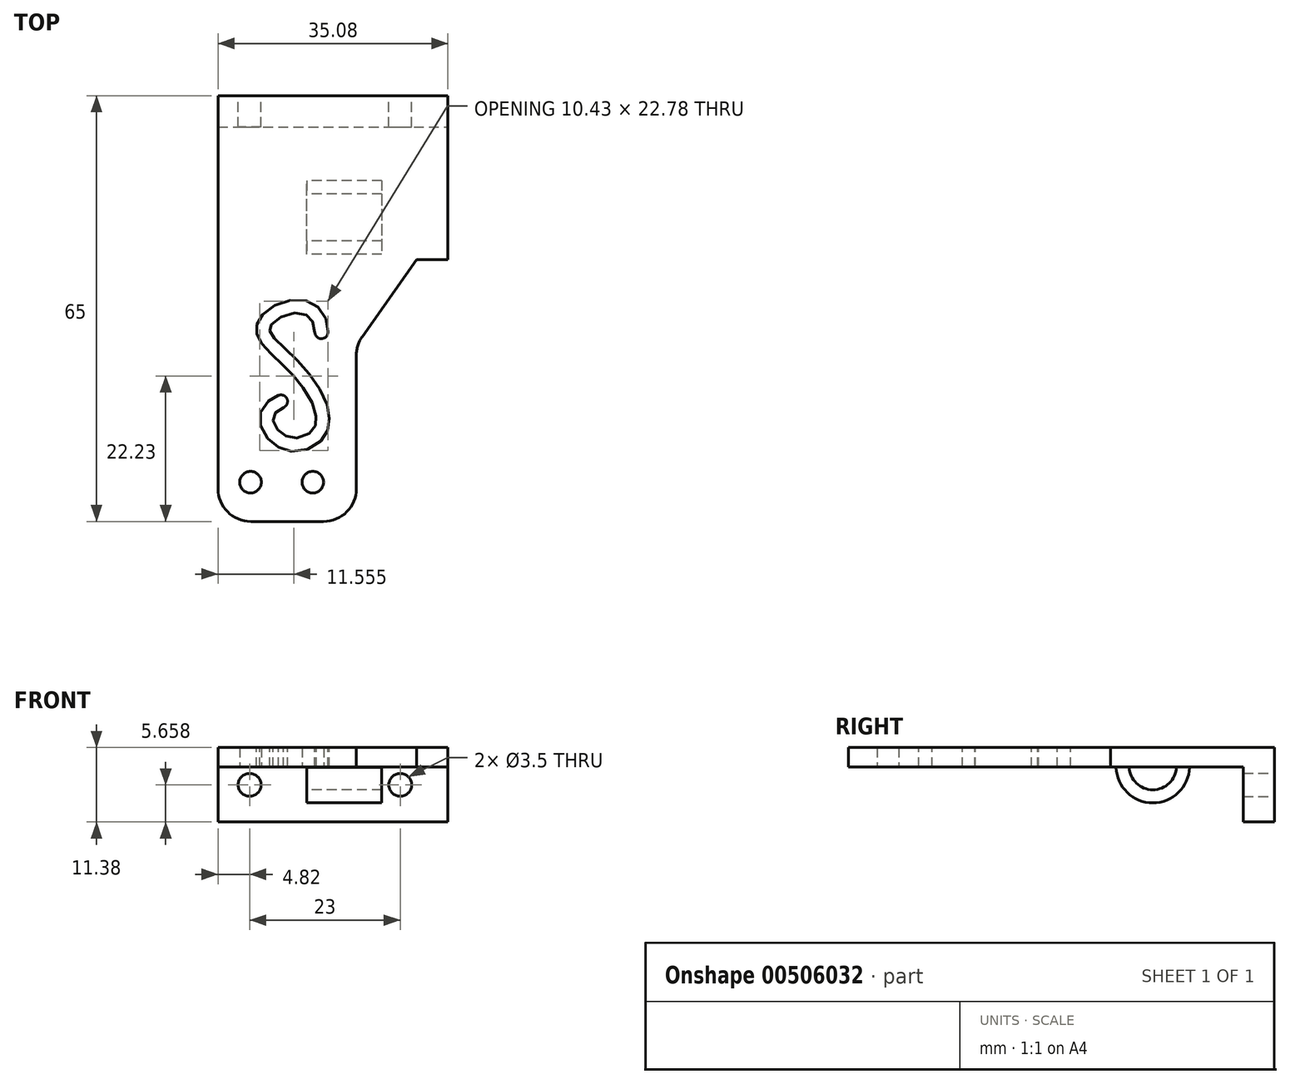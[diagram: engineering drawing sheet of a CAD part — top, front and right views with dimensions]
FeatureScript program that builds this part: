
annotation { "Feature Type Name" : "Feature", "Feature Type Description" : "" }
export const myFeature = defineFeature(function(context is Context, id is Id, definition is map)
    precondition{}
    {
        {
            var Q0;
            Q0=qCreatedBy(makeId("Top.planeOp"),FACE);
            var sketch = newSketch(context, id + "F0", { "sketchPlane" : qUnion([Q0])});
            skLineSegment(sketch, "E0", {"start": v(0, 7.37) * mm, "end": v(-30.32, 7.37) * mm});
            skLineSegment(sketch, "E1", {"start": v(-30.32, 7.37) * mm, "end": v(-30.32, -32.63) * mm});
            skLineSegment(sketch, "E2", {"start": v(-30.32, -32.63) * mm, "end": v(-9.2, -32.63) * mm});
            skLineSegment(sketch, "E3", {"start": v(-9.2, -32.63) * mm, "end": v(-9.2, -5.67) * mm});
            skLineSegment(sketch, "E4", {"start": v(-9.2, -5.67) * mm, "end": v(0, 7.37) * mm});
            skLineSegment(sketch, "E5", {"start": v(-25.36, -26.63) * mm, "end": v(-15.86, -26.63) * mm, "construction": true});
            skSolve(sketch);
        }
        {
            var Q0;
            Q0=makeQuery(id+"F0.imprint","IMPRINT",FACE,{"disambiguationData":[TD([[makeQuery(id+"F0.imprint","IMPRINT",EDGE,{"derivedFrom":sQuery(id+"F0.wireOp",EDGE,"E0")}),1.0]])]});
            extrude(context, id + "F1", {"entities" : qUnion([Q0]), "depth" : 3 * mm});
        }
        {
            var Q0;
            Q0=sQuery(id+"F0.wireOp",VERTEX,"b83b9fe4-897f-4c07-88cb-3c43593c5d40");
            var Q1;
            Q1=sQuery(id+"F0.wireOp",VERTEX,"b232d156-1ebf-488e-844c-e46001ad8d3b");
            var Q2;
            Q2=sQuery(id+"F0.wireOp",VERTEX,"E5.start");
            var Q3;
            Q3=sQuery(id+"F0.wireOp",VERTEX,"E5.end");
            var Q4;
            Q4=makeQuery(id+"F1.opExtrude","SWEPT_BODY",BODY,{"disambiguationData":[OSD([sQuery(id+"F0.wireOp",EDGE,"E0"),sQuery(id+"F0.wireOp",EDGE,"E1"),sQuery(id+"F0.wireOp",EDGE,"E2"),sQuery(id+"F0.wireOp",EDGE,"E3"),sQuery(id+"F0.wireOp",EDGE,"E4")])]});
            hole(context, id + "F2", {"style" : HoleStyle.SIMPLE, "endStyle" : HoleEndStyle.BLIND, "oppositeDirection" : true, "standardTappedOrClearance" : lookupTablePath({ "standard" : "ISO", "fit" : "Normal", "size" : "M3", "type" : "Clearance" }), "standardBlindInLast" : lookupTablePath({ "fit" : "Standard", "standard" : "ISO", "size" : "M3", "type" : "Clearance" }), "holeDiameter" : 3.3 * mm, "holeDepth" : 18 * mm, "isTappedThrough" : true, "tappedDepth" : 12 * mm, "tapClearance" : 3, "startFromSketch" : true, "locations" : qUnion([Q0, Q1, Q2, Q3]), "scope" : qUnion([Q4])});
        }
        {
            var Q0;
            Q0=makeQuery(id+"F1.opExtrude","SWEPT_EDGE",EDGE,{"disambiguationData":[OSD([sQuery(id+"F0.wireOp",EDGE,"E2"),sQuery(id+"F0.wireOp",EDGE,"E3")])]});
            var Q1;
            Q1=makeQuery(id+"F1.opExtrude","SWEPT_EDGE",EDGE,{"disambiguationData":[OSD([sQuery(id+"F0.wireOp",EDGE,"E1"),sQuery(id+"F0.wireOp",EDGE,"E2")])]});
            fillet(context, id + "F3", {"entities" : qUnion([Q0, Q1]), "radius" : 5 * mm, "tangentPropagation" : true, "allowEdgeOverflow" : false});
        }
        {
            var Q0;
            Q0=makeQuery(id+"F1.opExtrude","CAP_FACE",FACE,{"disambiguationData":[OSD([sQuery(id+"F0.wireOp",EDGE,"E0"),sQuery(id+"F0.wireOp",EDGE,"E1"),sQuery(id+"F0.wireOp",EDGE,"E2"),sQuery(id+"F0.wireOp",EDGE,"E3"),sQuery(id+"F0.wireOp",EDGE,"E4")])],"isStart":false});
            var sketch = newSketch(context, id + "F4", { "sketchPlane" : qUnion([Q0])});
            skFitSpline(sketch, "E6", {"points": [v(-14.55, -3.72) * mm, v(-19.67, 0) * mm, v(-23.45, -3.28) * mm, v(-18.59, -9.14) * mm, v(-14.59, -18.4) * mm, v(-20.53, -20.4) * mm, v(-20.71, -14.3) * mm], "startDerivative": vector(-4.14, 69.45) * mm, "endDerivative": vector(70.56, 28.51) * mm});
            skArc(sketch, "E7.0.startCap", {"start": v(-13.55, -3.66) * mm, "mid": v(-14.5, -4.72) * mm, "end": v(-15.55, -3.78) * mm});
            skArc(sketch, "E7.0.endCap", {"start": v(-21.09, -13.38) * mm, "mid": v(-19.79, -13.93) * mm, "end": v(-20.34, -15.23) * mm});
            skFitSpline(sketch, "E7.0.left", {"points": [v(-15.55, -3.78) * mm, v(-15.59, -3.14) * mm, v(-15.76, -2.4) * mm, v(-16.11, -1.76) * mm, v(-16.42, -1.4) * mm, v(-16.76, -1.15) * mm, v(-17.3, -0.9) * mm, v(-18.13, -0.76) * mm, v(-19.27, -0.9) * mm, v(-20.4, -1.26) * mm, v(-21.37, -1.8) * mm, v(-21.96, -2.33) * mm, v(-22.26, -2.73) * mm, v(-22.4, -3) * mm, v(-22.45, -3.23) * mm, v(-22.45, -3.4) * mm, v(-22.4, -3.63) * mm, v(-22.24, -3.94) * mm, v(-22, -4.32) * mm, v(-21.54, -4.87) * mm, v(-20.75, -5.66) * mm, v(-19.59, -6.74) * mm, v(-18.3, -7.96) * mm, v(-17.02, -9.36) * mm, v(-15.82, -10.88) * mm, v(-14.78, -12.48) * mm, v(-13.96, -14.12) * mm, v(-13.51, -15.5) * mm, v(-13.35, -16.6) * mm, v(-13.34, -17.43) * mm, v(-13.46, -18.24) * mm, v(-13.74, -19.03) * mm, v(-14.17, -19.74) * mm, v(-14.9, -20.56) * mm, v(-16.02, -21.35) * mm, v(-17.63, -21.87) * mm, v(-19.07, -21.9) * mm, v(-20.23, -21.63) * mm, v(-21.08, -21.27) * mm, v(-21.86, -20.76) * mm, v(-22.79, -19.9) * mm, v(-23.5, -18.85) * mm, v(-23.88, -17.63) * mm, v(-23.94, -16.65) * mm, v(-23.7, -15.65) * mm, v(-23.14, -14.72) * mm, v(-22.27, -13.95) * mm, v(-21.51, -13.55) * mm, v(-21.09, -13.38) * mm]});
            skFitSpline(sketch, "E7.0.right", {"points": [v(-13.55, -3.66) * mm, v(-13.6, -2.85) * mm, v(-13.83, -1.77) * mm, v(-14.44, -0.63) * mm, v(-15.04, 0.07) * mm, v(-15.74, 0.6) * mm, v(-16.77, 1.06) * mm, v(-18.13, 1.26) * mm, v(-19.72, 1.07) * mm, v(-21.2, 0.59) * mm, v(-22.5, -0.14) * mm, v(-23.4, -0.92) * mm, v(-23.96, -1.66) * mm, v(-24.27, -2.27) * mm, v(-24.42, -2.84) * mm, v(-24.45, -3.32) * mm, v(-24.42, -3.8) * mm, v(-24.27, -4.36) * mm, v(-23.97, -4.97) * mm, v(-23.59, -5.53) * mm, v(-23, -6.24) * mm, v(-22.12, -7.12) * mm, v(-20.95, -8.2) * mm, v(-19.93, -9.18) * mm, v(-19.13, -10.01) * mm, v(-18.36, -10.89) * mm, v(-17.45, -12.05) * mm, v(-16.51, -13.48) * mm, v(-15.8, -14.9) * mm, v(-15.46, -16) * mm, v(-15.35, -16.77) * mm, v(-15.34, -17.3) * mm, v(-15.41, -17.76) * mm, v(-15.56, -18.16) * mm, v(-15.79, -18.55) * mm, v(-16.2, -19.03) * mm, v(-16.92, -19.53) * mm, v(-17.97, -19.87) * mm, v(-18.9, -19.89) * mm, v(-19.6, -19.72) * mm, v(-20.12, -19.5) * mm, v(-20.62, -19.17) * mm, v(-21.09, -18.75) * mm, v(-21.47, -18.26) * mm, v(-21.75, -17.75) * mm, v(-21.9, -17.26) * mm, v(-21.92, -16.81) * mm, v(-21.82, -16.42) * mm, v(-21.6, -16.04) * mm, v(-21.15, -15.63) * mm, v(-20.65, -15.35) * mm, v(-20.34, -15.23) * mm]});
            skSolve(sketch);
        }
        {
            var Q0;
            Q0 = qSketchRegion(id + "F4", true);
            extrude(context, id + "F5", {"entities" : qUnion([Q0]), "operationType" : NewBodyOperationType.REMOVE, "oppositeDirection" : true, "depth" : 25 * mm});
        }
        {
            var Q0;
            Q0=makeQuery(id+"F1.opExtrude","SWEPT_EDGE",EDGE,{"disambiguationData":[OSD([sQuery(id+"F0.wireOp",EDGE,"E3"),sQuery(id+"F0.wireOp",EDGE,"E4")])]});
            fillet(context, id + "F6", {"entities" : qUnion([Q0]), "radius" : 5 * mm, "tangentPropagation" : true, "allowEdgeOverflow" : false});
        }
        {
            var Q0;
            Q0=makeQuery(id+"F1.opExtrude","SWEPT_FACE",FACE,{"disambiguationData":[OSD([sQuery(id+"F0.wireOp",EDGE,"E0")])]});
            var sketch = newSketch(context, id + "F7", { "sketchPlane" : qUnion([Q0])});
            skLineSegment(sketch, "E8.bottom", {"start": v(-4.76, 3) * mm, "end": v(30.32, 3) * mm});
            skLineSegment(sketch, "E8.top", {"start": v(-4.76, -8.38) * mm, "end": v(30.32, -8.38) * mm});
            skLineSegment(sketch, "E8.left", {"start": v(-4.76, 3) * mm, "end": v(-4.76, -8.38) * mm});
            skLineSegment(sketch, "E8.right", {"start": v(30.32, 3) * mm, "end": v(30.32, -8.38) * mm});
            skSolve(sketch);
        }
        {
            var Q0;
            Q0 = qSketchRegion(id + "F7", true);
            extrude(context, id + "F8", {"entities" : qUnion([Q0]), "operationType" : NewBodyOperationType.ADD, "depth" : 25 * mm, "offsetDistance" : 25 * mm});
        }
        {
            var Q0;
            Q0=makeQuery(id+"F8.opExtrude","SWEPT_FACE",FACE,{"disambiguationData":[OSD([sQuery(id+"F7.wireOp",EDGE,"E8.left")])]});
            var sketch = newSketch(context, id + "F9", { "sketchPlane" : qUnion([Q0])});
            skLineSegment(sketch, "E9", {"start": v(27.6, -8.38) * mm, "end": v(27.6, 0) * mm});
            skLineSegment(sketch, "E10", {"start": v(27.6, 0) * mm, "end": v(7.37, 0) * mm});
            skLineSegment(sketch, "E11", {"start": v(7.37, 0) * mm, "end": v(27.6, -8.38) * mm});
            skSolve(sketch);
        }
        {
            var Q0;
            Q0=makeQuery(id+"F9.imprint","IMPRINT",FACE,{"disambiguationData":[TD([[makeQuery(id+"F9.imprint","IMPRINT",EDGE,{"derivedFrom":sQuery(id+"F9.wireOp",EDGE,"E9")}),1.0]])]});
            var Q1;
            {var subQ0=sQuery(id+"F9.wireOp",EDGE,"E11");Q1=makeQuery(id+"F9.imprint","IMPRINT",FACE,{"disambiguationData":[TD([[makeQuery(id+"F9.imprint","IMPRINT",EDGE,{"derivedFrom":subQ0}),-1.0]])]});}
            extrude(context, id + "F10", {"entities" : qUnion([Q0, Q1]), "operationType" : NewBodyOperationType.REMOVE, "oppositeDirection" : true, "depth" : 40 * mm, "offsetDistance" : 25 * mm});
        }
        {
            var Q0;
            Q0=makeQuery(id+"F8.opExtrude","CAP_FACE",FACE,{"disambiguationData":[OSD([sQuery(id+"F7.wireOp",EDGE,"E8.bottom"),sQuery(id+"F7.wireOp",EDGE,"E8.top"),sQuery(id+"F7.wireOp",EDGE,"E8.left"),sQuery(id+"F7.wireOp",EDGE,"E8.right")])],"isStart":false});
            var sketch = newSketch(context, id + "F11", { "sketchPlane" : qUnion([Q0])});
            skPoint(sketch, "E12", {"position": v(2.5, -2.72) * mm});
            skPoint(sketch, "E13", {"position": v(25.5, -2.72) * mm});
            skSolve(sketch);
        }
        {
            var Q0;
            Q0=sQuery(id+"F11.wireOp",VERTEX,"E13");
            var Q1;
            Q1=sQuery(id+"F11.wireOp",VERTEX,"E12");
            var Q2;
            Q2=makeQuery(id+"F1.opExtrude","SWEPT_BODY",BODY,{"disambiguationData":[OSD([sQuery(id+"F0.wireOp",EDGE,"E0"),sQuery(id+"F0.wireOp",EDGE,"E1"),sQuery(id+"F0.wireOp",EDGE,"E2"),sQuery(id+"F0.wireOp",EDGE,"E3"),sQuery(id+"F0.wireOp",EDGE,"E4")])]});
            hole(context, id + "F12", {"style" : HoleStyle.SIMPLE, "endStyle" : HoleEndStyle.BLIND, "holeDiameter" : 3.5 * mm, "holeDepth" : 25 * mm, "isTappedThrough" : true, "tappedDepth" : 12 * mm, "tapClearance" : 3, "locations" : qUnion([Q0, Q1]), "scope" : qUnion([Q2])});
        }
        {
            var Q0;
            Q0=makeQuery(id+"F8.boolean.opBoolean","MERGE",FACE,{"derivedFrom":[makeQuery(id+"F1.opExtrude","SWEPT_FACE",FACE,{"disambiguationData":[OSD([sQuery(id+"F0.wireOp",EDGE,"E1")])]}),makeQuery(id+"F8.opExtrude","SWEPT_FACE",FACE,{"disambiguationData":[OSD([sQuery(id+"F7.wireOp",EDGE,"E8.right")])]})]});
            var sketch = newSketch(context, id + "F13", { "sketchPlane" : qUnion([Q0])});
            skArc(sketch, "E14", {"start": v(-17.4, 0) * mm, "mid": v(-13.8, -3.48) * mm, "end": v(-10.2, 0) * mm});
            skArc(sketch, "E15.0", {"start": v(-19.4, -0.04) * mm, "mid": v(-13.8, -5.48) * mm, "end": v(-8.2, -0.04) * mm});
            skLineSegment(sketch, "E16", {"start": v(-19.4, -0.04) * mm, "end": v(-17.4, 0) * mm});
            skLineSegment(sketch, "E17", {"start": v(-10.2, 0) * mm, "end": v(-8.2, -0.04) * mm});
            skSolve(sketch);
        }
        {
            var Q0;
            Q0=makeQuery(id+"F13.imprint","IMPRINT",FACE,{"disambiguationData":[TD([[makeQuery(id+"F13.imprint","IMPRINT",EDGE,{"derivedFrom":sQuery(id+"F13.wireOp",EDGE,"E14")}),-1.0]])]});
            extrude(context, id + "F14", {"entities" : qUnion([Q0]), "oppositeDirection" : true, "depth" : 25 * mm, "offsetDistance" : 25 * mm});
        }
        {
            var Q0;
            Q0=makeQuery(id+"F10.boolean.opBoolean","MERGE",FACE,{"derivedFrom":[makeQuery(id+"F1.opExtrude","CAP_FACE",FACE,{"disambiguationData":[OSD([sQuery(id+"F0.wireOp",EDGE,"E0"),sQuery(id+"F0.wireOp",EDGE,"E1"),sQuery(id+"F0.wireOp",EDGE,"E2"),sQuery(id+"F0.wireOp",EDGE,"E3"),sQuery(id+"F0.wireOp",EDGE,"E4")])],"isStart":true}),makeQuery(id+"F10.opExtrude","SWEPT_FACE",FACE,{"disambiguationData":[OSD([sQuery(id+"F9.wireOp",EDGE,"E10")])]})]});
            var sketch = newSketch(context, id + "F15", { "sketchPlane" : qUnion([Q0])});
            skLineSegment(sketch, "E18.bottom", {"start": v(-30.32, -4.34) * mm, "end": v(-16.75, -4.34) * mm});
            skLineSegment(sketch, "E18.top", {"start": v(-30.32, -25.38) * mm, "end": v(-16.75, -25.38) * mm});
            skLineSegment(sketch, "E18.left", {"start": v(-30.32, -4.34) * mm, "end": v(-30.32, -25.38) * mm});
            skLineSegment(sketch, "E18.right", {"start": v(-16.75, -4.34) * mm, "end": v(-16.75, -25.38) * mm});
            skSolve(sketch);
        }
        {
            var Q0;
            Q0 = qSketchRegion(id + "F15", true);
            extrude(context, id + "F16", {"entities" : qUnion([Q0]), "operationType" : NewBodyOperationType.REMOVE, "depth" : 25 * mm, "offsetDistance" : 25 * mm});
        }
    });
